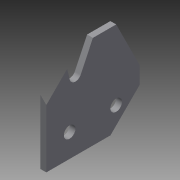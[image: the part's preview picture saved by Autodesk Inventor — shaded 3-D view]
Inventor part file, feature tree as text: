
AUTODESK INVENTOR PART (.ipt)
format: ipt  version: 2015 SP1 (Build 190203100, 203)  size: 96,256 bytes
history: native  units: in
note: dims shown in document units (in); Inventor stores cm internally (conversion verified against a paired STEP export)
features: sketch x2, extrude x1, hole x1
ambient origin geometry x8: Origin, YZ Plane, XZ Plane, XY Plane, X Axis, Y Axis, Z Axis, Center Point
bodies: Solid1 (feature_tree)
feature tree (4):
  extrude  "Extrusion1"  Depth=2.0in
  hole  "Hole1"  [1 undecoded]
  sketch  "Sketch1"  dims[d0=2.0in d1=2.0in]
  sketch  "Sketch2"  dims[d2=0.375in d3=0.5in d6=0.25in d7=0.5in d8=0.625in d9=0.125in d10=0.0in d11=0.5in d12=0.5in d13=0.5in d14=1.5in d15=0.25in d16=0.75in d17=0.375in d18=0.25in d19=0.5635in d20=1.0in d21=0.8108in d22=1.0in d23=0.5in]
note: 1 required parameter value undecoded (feature->parameter linkage not recoverable at this tier; creation-order binding heuristic only, values carry confidence <= 0.55)
